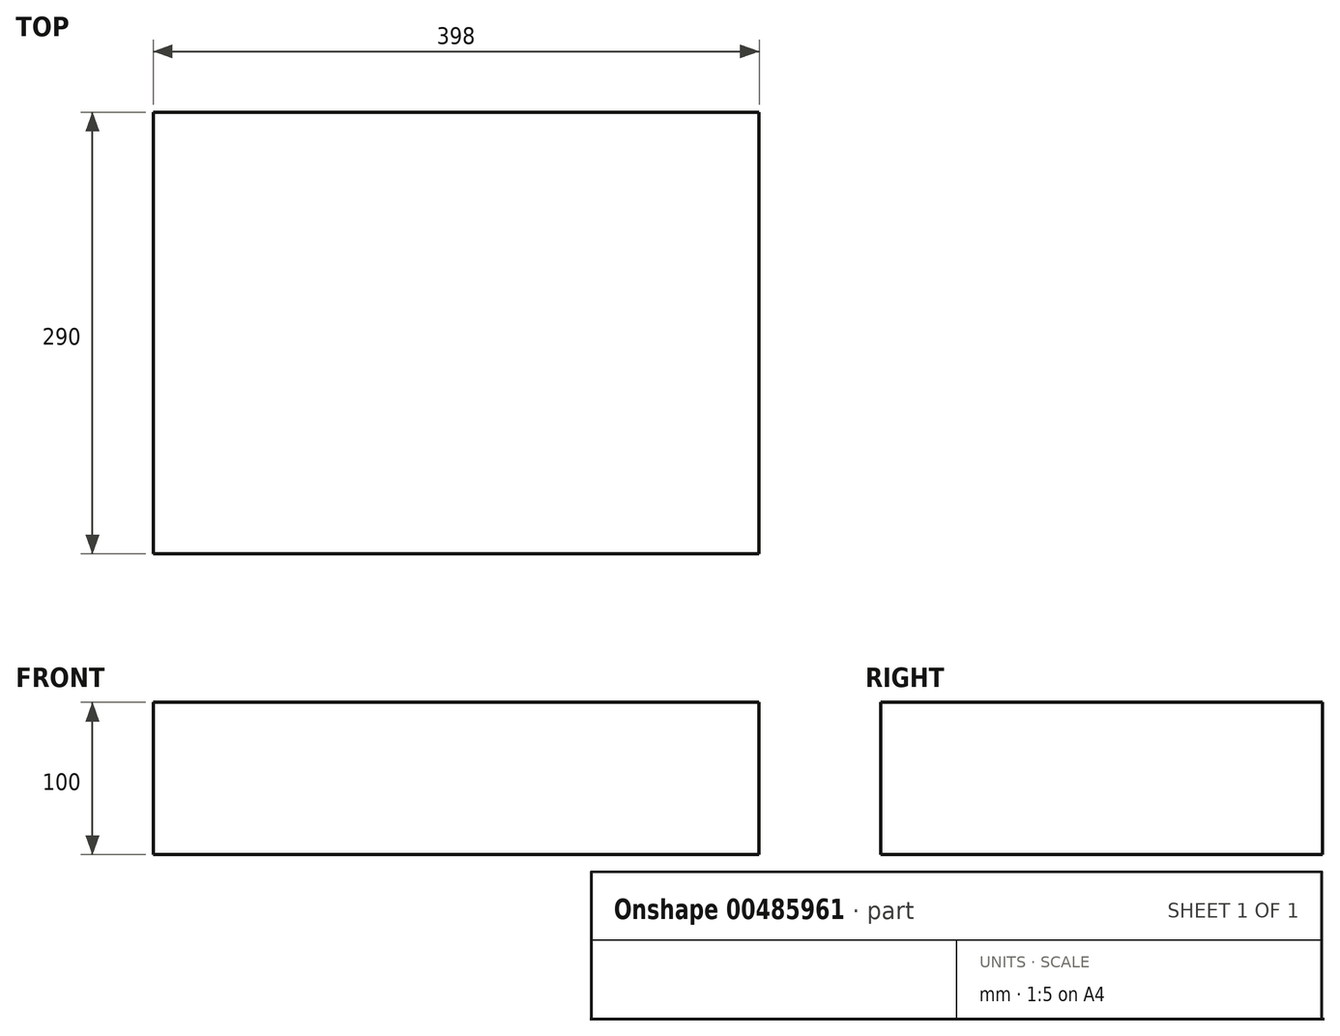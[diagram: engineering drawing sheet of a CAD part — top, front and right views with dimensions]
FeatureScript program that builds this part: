
annotation { "Feature Type Name" : "Feature", "Feature Type Description" : "" }
export const myFeature = defineFeature(function(context is Context, id is Id, definition is map)
    precondition{}
    {
        {
            var Q0;
            Q0=qCreatedBy(makeId("Top.planeOp"),FACE);
            var sketch = newSketch(context, id + "F0", { "sketchPlane" : qUnion([Q0])});
            skLineSegment(sketch, "E0.bottom", {"start": v(-177.7, 177.64) * mm, "end": v(220.3, 177.64) * mm});
            skLineSegment(sketch, "E0.top", {"start": v(-177.7, -112.36) * mm, "end": v(220.3, -112.36) * mm});
            skLineSegment(sketch, "E0.left", {"start": v(-177.7, 177.64) * mm, "end": v(-177.7, -112.36) * mm});
            skLineSegment(sketch, "E0.right", {"start": v(220.3, 177.64) * mm, "end": v(220.3, -112.36) * mm});
            skSolve(sketch);
        }
        {
            var Q0;
            Q0=makeQuery(id+"F0.imprint","IMPRINT",FACE,{"disambiguationData":[TD([[makeQuery(id+"F0.imprint","IMPRINT",EDGE,{"derivedFrom":sQuery(id+"F0.wireOp",EDGE,"E0.bottom")}),-1.0]])]});
            var Q1;
            Q1=sQuery(id+"F0.wireOp",EDGE,"E0.bottom");
            extrude(context, id + "F1", {"entities" : qUnion([Q0]), "surfaceEntities" : qUnion([Q1]), "depth" : 100 * mm});
        }
    });
